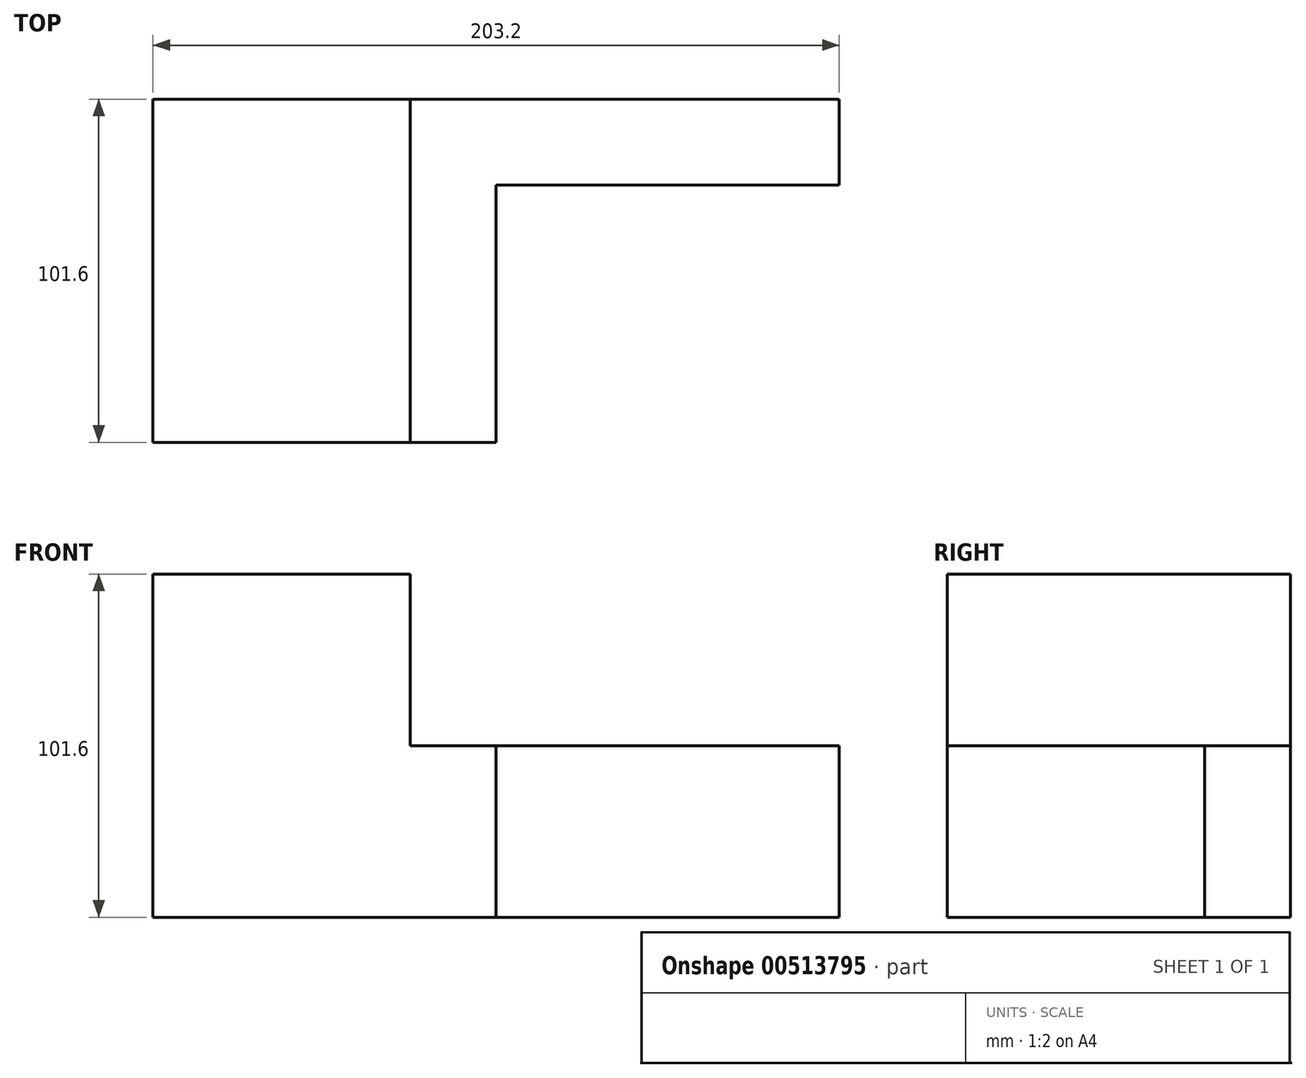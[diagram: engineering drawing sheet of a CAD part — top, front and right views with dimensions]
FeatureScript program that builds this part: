
annotation { "Feature Type Name" : "Feature", "Feature Type Description" : "" }
export const myFeature = defineFeature(function(context is Context, id is Id, definition is map)
    precondition{}
    {
        {
            var Q0;
            Q0=qCreatedBy(makeId("Front.planeOp"),FACE);
            var sketch = newSketch(context, id + "F0", { "sketchPlane" : qUnion([Q0])});
            skLineSegment(sketch, "E0.bottom", {"start": v(-96.43, 47.83) * mm, "end": v(-20.23, 47.83) * mm});
            skLineSegment(sketch, "E0.top", {"start": v(-96.43, -53.77) * mm, "end": v(5.17, -53.77) * mm});
            skLineSegment(sketch, "E0.left", {"start": v(-96.43, 47.83) * mm, "end": v(-96.43, -53.77) * mm});
            skLineSegment(sketch, "E1", {"start": v(106.77, -2.97) * mm, "end": v(106.77, -53.77) * mm});
            skLineSegment(sketch, "E2", {"start": v(-20.23, 47.83) * mm, "end": v(-20.23, -2.97) * mm});
            skLineSegment(sketch, "E3", {"start": v(-20.23, -2.97) * mm, "end": v(11.26, -2.97) * mm});
            skLineSegment(sketch, "E4", {"start": v(11.26, -2.97) * mm, "end": v(106.77, -2.97) * mm});
            skLineSegment(sketch, "E5", {"start": v(5.17, -53.77) * mm, "end": v(106.77, -53.77) * mm});
            skSolve(sketch);
        }
        {
            var Q0;
            Q0=qSketchRegion(id+"F0",true);
            extrude(context, id + "F1", {"entities" : qUnion([Q0]), "depth" : 101.6 * mm});
        }
        {
            var Q0;
            Q0=makeQuery(id+"F1.opExtrude","SWEPT_FACE",FACE,{"disambiguationData":[OSD([sQuery(id+"F0.wireOp",EDGE,"E3"),sQuery(id+"F0.wireOp",EDGE,"E4")])]});
            var sketch = newSketch(context, id + "F2", { "sketchPlane" : qUnion([Q0])});
            skLineSegment(sketch, "E6.bottom", {"start": v(5.17, -25.4) * mm, "end": v(106.77, -25.4) * mm});
            skLineSegment(sketch, "E6.top", {"start": v(5.17, -101.6) * mm, "end": v(106.77, -101.6) * mm});
            skLineSegment(sketch, "E6.left", {"start": v(5.17, -25.4) * mm, "end": v(5.17, -101.6) * mm});
            skLineSegment(sketch, "E6.right", {"start": v(106.77, -25.4) * mm, "end": v(106.77, -101.6) * mm});
            skSolve(sketch);
        }
        {
            var Q0;
            Q0=makeQuery(id+"F2.imprint","IMPRINT",FACE,{"disambiguationData":[TD([[makeQuery(id+"F2.imprint","IMPRINT",EDGE,{"derivedFrom":sQuery(id+"F2.wireOp",EDGE,"E6.bottom")}),-1.0]])]});
            extrude(context, id + "F3", {"entities" : qUnion([Q0]), "operationType" : NewBodyOperationType.REMOVE, "oppositeDirection" : true, "depth" : 76.2 * mm});
        }
    });
